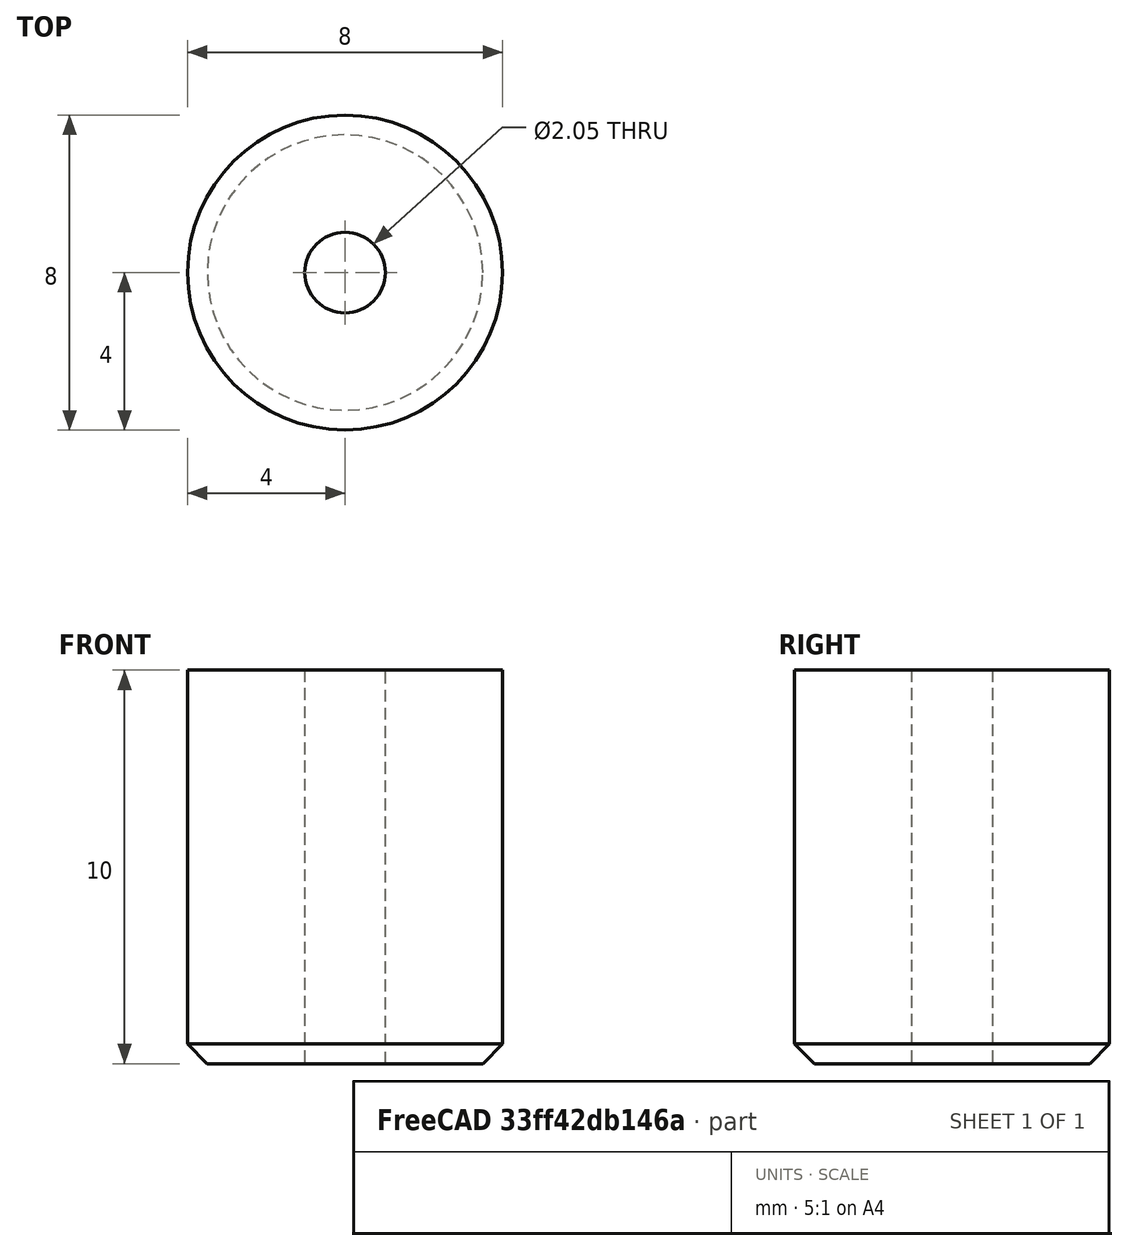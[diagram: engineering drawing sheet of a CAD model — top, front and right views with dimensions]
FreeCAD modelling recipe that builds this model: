
FCSTD DOCUMENT  (FreeCAD 1.1R41365 (Git))
Label: rod_collet
License: All rights reserved
LicenseURL: https://en.wikipedia.org/wiki/All_rights_reserved
objects: App::Point×1, Sketcher::SketchObject×1, PartDesign::Pad×1, PartDesign::Chamfer×1, PartDesign::Body×1
note: 9 computed .brp shape members not serialized (recipe doc carries the construction recipe); baked Part::Feature solids carry a one-line shape summary decoded from their .brp

FEATURE [App::Point] Origin001
  Role = Origin
FEATURE [Sketcher::SketchObject] Sketch
  ArcFitTolerance = 1e-06
  AttachmentSupport = -> [Origin]
  ExternalTypes = [0]
  FullyConstrained = true
  MakeInternals = false
  MapMode = 5
  sketch-geometry (2):
    g0: Circle CenterX=0 CenterY=0 CenterZ=0 NormalX=0 NormalY=0 NormalZ=1 AngleXU=0 Radius=4
    g1: Circle CenterX=0 CenterY=0 CenterZ=0 NormalX=0 NormalY=0 NormalZ=1 AngleXU=0 Radius=1.025
  constraints (4):
    c: Coincident(g0,g-1)
    c: Coincident(g1,g0)
    c: Diameter(g0) = 8
    c: Diameter(g1) = 2.05
FEATURE [PartDesign::Pad] Pad
  Direction = (0,0,1)
  Length = 10
  Length2 = 10
  Profile = -> Sketch
  ReferenceAxis = -> Sketch [N_Axis]
  Refine = true
  Suppressed = false
  Type = 0
FEATURE [PartDesign::Chamfer] Chamfer
  Angle = 45
  Base = -> Pad [Edge2]
  BaseFeature = -> Pad
  ChamferType = 0
  FlipDirection = false
  Refine = true
  Size = 0.5
  Size2 = 1
  SupportTransform = false
  Suppressed = false
  UseAllEdges = false
FEATURE [PartDesign::Body] Body  label="rod_collet"
  AllowCompound = false
  Group = -> [Sketch,Pad,Chamfer]
  Origin = -> Origin
  Tip = -> Chamfer
